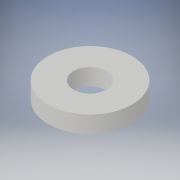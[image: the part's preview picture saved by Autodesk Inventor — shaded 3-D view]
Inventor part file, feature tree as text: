
AUTODESK INVENTOR PART (.ipt)
format: ipt  version: 2017 (Build 210142000, 142)  size: 93,696 bytes
history: native  units: in
note: dims shown in document units (in); Inventor stores cm internally (conversion verified against a paired STEP export)
features: extrude x1, sketch x1
ambient origin geometry x8: Origin, YZ Plane, XZ Plane, XY Plane, X Axis, Y Axis, Z Axis, Center Point
bodies: Solid1 (feature_tree)
feature tree (2):
  extrude  "Extrusion1"  Depth=0.1in
  sketch  "Sketch1"  dims[d0=0.194in d1=0.5in d2=0.1in d3=0.0in]
